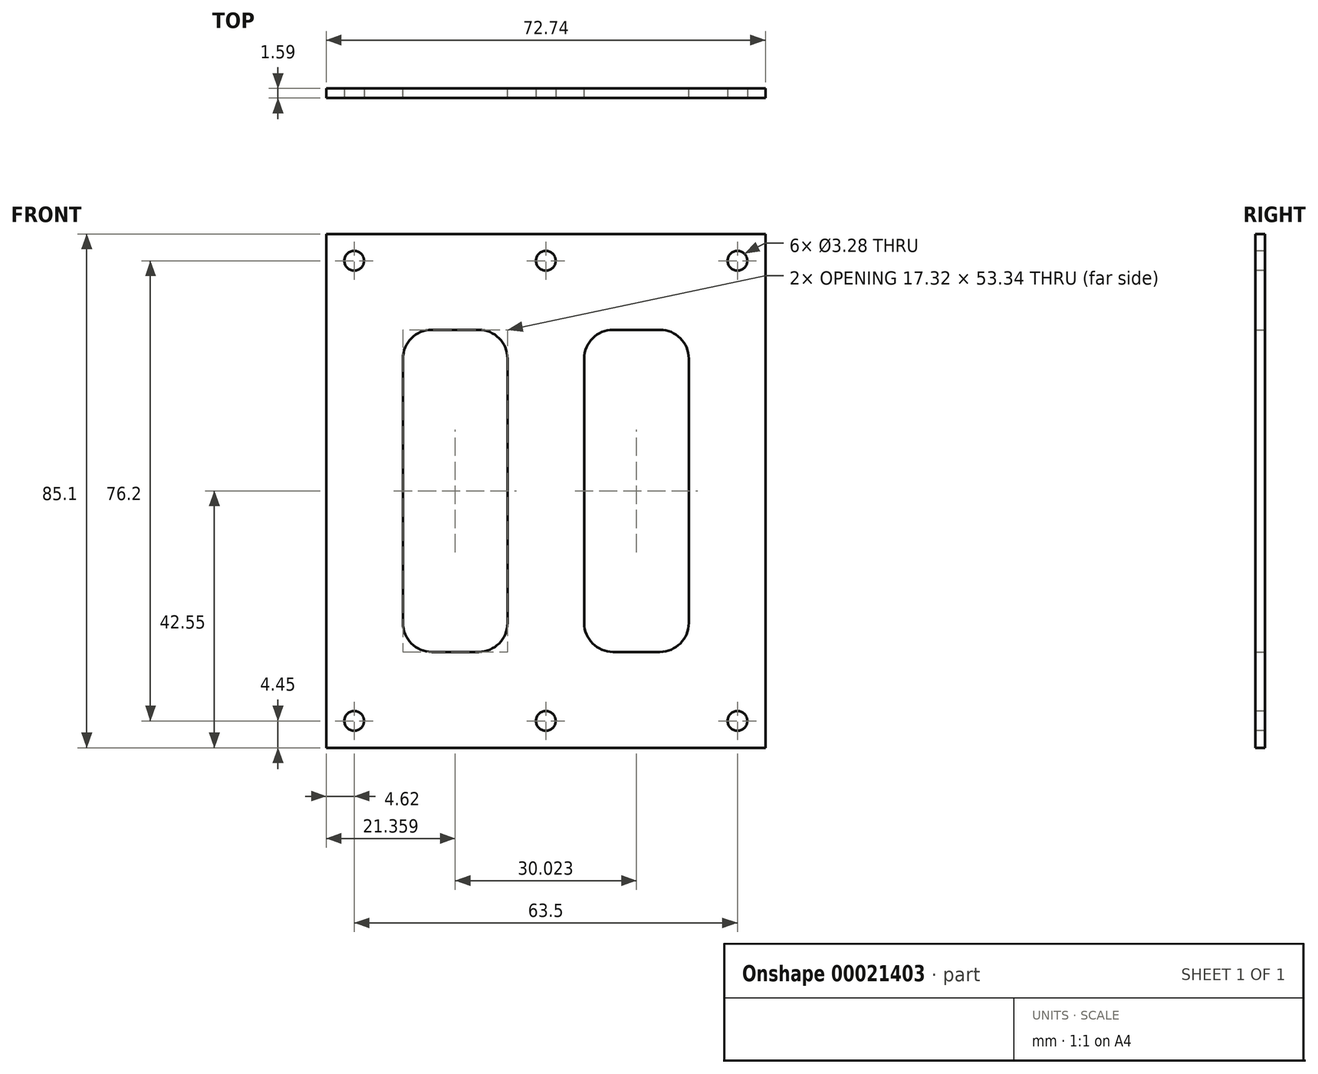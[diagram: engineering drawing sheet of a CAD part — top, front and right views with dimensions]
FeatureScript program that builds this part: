
annotation { "Feature Type Name" : "Feature", "Feature Type Description" : "" }
export const myFeature = defineFeature(function(context is Context, id is Id, definition is map)
    precondition{}
    {
        {
            var Q0;
            Q0=qCreatedBy(makeId("Front.planeOp"),FACE);
            var sketch = newSketch(context, id + "F0", { "sketchPlane" : qUnion([Q0])});
            skLineSegment(sketch, "E0.rect.bottom", {"start": v(-36.37, 42.55) * mm, "end": v(36.37, 42.55) * mm});
            skLineSegment(sketch, "E0.rect.top", {"start": v(-36.37, -42.55) * mm, "end": v(36.37, -42.55) * mm});
            skLineSegment(sketch, "E0.rect.left", {"start": v(-36.37, 42.55) * mm, "end": v(-36.37, -42.55) * mm});
            skLineSegment(sketch, "E0.rect.right", {"start": v(36.37, 42.55) * mm, "end": v(36.37, -42.55) * mm});
            skPoint(sketch, "E0.rect.middle", {"position": v(0, 0) * mm});
            skLineSegment(sketch, "E1.bottom", {"start": v(-23.67, 26.67) * mm, "end": v(-6.35, 26.67) * mm});
            skLineSegment(sketch, "E1.top", {"start": v(-23.67, -26.67) * mm, "end": v(-6.35, -26.67) * mm});
            skLineSegment(sketch, "E1.left", {"start": v(-23.67, 26.67) * mm, "end": v(-23.67, -26.67) * mm});
            skLineSegment(sketch, "E1.right", {"start": v(-6.35, 26.67) * mm, "end": v(-6.35, -26.67) * mm});
            skLineSegment(sketch, "E2.bottom", {"start": v(6.35, 26.67) * mm, "end": v(23.67, 26.67) * mm});
            skLineSegment(sketch, "E2.top", {"start": v(6.35, -26.67) * mm, "end": v(23.67, -26.67) * mm});
            skLineSegment(sketch, "E2.left", {"start": v(6.35, 26.67) * mm, "end": v(6.35, -26.67) * mm});
            skLineSegment(sketch, "E2.right", {"start": v(23.67, 26.67) * mm, "end": v(23.67, -26.67) * mm});
            skLineSegment(sketch, "E3", {"start": v(0, 0) * mm, "end": v(0, 48.33) * mm});
            skLineSegment(sketch, "E4", {"start": v(0, 0) * mm, "end": v(44.84, 0) * mm});
            skSolve(sketch);
        }
        {
            var Q0;
            {var subQ12=sQuery(id+"F0.wireOp",EDGE,"E0.rect.top");Q0=makeQuery(id+"F0.imprint","IMPRINT",FACE,{"disambiguationData":[TD([[makeQuery(id+"F0.imprint","IMPRINT",EDGE,{"derivedFrom":subQ12}),1.0]])]});}
            var Q1;
            {var subQ7=sQuery(id+"F0.wireOp",EDGE,"E2.bottom");Q1=makeQuery(id+"F0.imprint","IMPRINT",FACE,{"disambiguationData":[TD([[makeQuery(id+"F0.imprint","IMPRINT",EDGE,{"derivedFrom":subQ7}),1.0]])]});}
            extrude(context, id + "F1", {"entities" : qUnion([Q0, Q1]), "depth" : 1.59 * mm});
        }
        {
            var Q0;
            Q0=makeQuery(id+"F1.opExtrude","SWEPT_EDGE",EDGE,{"disambiguationData":[OSD([sQuery(id+"F0.wireOp",EDGE,"E2.bottom"),sQuery(id+"F0.wireOp",EDGE,"E2.right")])]});
            var Q1;
            Q1=makeQuery(id+"F1.opExtrude","SWEPT_EDGE",EDGE,{"disambiguationData":[OSD([sQuery(id+"F0.wireOp",EDGE,"E1.bottom"),sQuery(id+"F0.wireOp",EDGE,"E1.right")])]});
            var Q2;
            Q2=makeQuery(id+"F1.opExtrude","SWEPT_EDGE",EDGE,{"disambiguationData":[OSD([sQuery(id+"F0.wireOp",EDGE,"E2.bottom"),sQuery(id+"F0.wireOp",EDGE,"E2.left")])]});
            var Q3;
            Q3=makeQuery(id+"F1.opExtrude","SWEPT_EDGE",EDGE,{"disambiguationData":[OSD([sQuery(id+"F0.wireOp",EDGE,"E1.bottom"),sQuery(id+"F0.wireOp",EDGE,"E1.left")])]});
            var Q4;
            Q4=makeQuery(id+"F1.opExtrude","SWEPT_EDGE",EDGE,{"disambiguationData":[OSD([sQuery(id+"F0.wireOp",EDGE,"E2.top"),sQuery(id+"F0.wireOp",EDGE,"E2.right")])]});
            var Q5;
            Q5=makeQuery(id+"F1.opExtrude","SWEPT_EDGE",EDGE,{"disambiguationData":[OSD([sQuery(id+"F0.wireOp",EDGE,"E1.top"),sQuery(id+"F0.wireOp",EDGE,"E1.left")])]});
            var Q6;
            Q6=makeQuery(id+"F1.opExtrude","SWEPT_EDGE",EDGE,{"disambiguationData":[OSD([sQuery(id+"F0.wireOp",EDGE,"E2.top"),sQuery(id+"F0.wireOp",EDGE,"E2.left")])]});
            var Q7;
            Q7=makeQuery(id+"F1.opExtrude","SWEPT_EDGE",EDGE,{"disambiguationData":[OSD([sQuery(id+"F0.wireOp",EDGE,"E1.top"),sQuery(id+"F0.wireOp",EDGE,"E1.right")])]});
            fillet(context, id + "F2", {"entities" : qUnion([Q0, Q1, Q2, Q3, Q4, Q5, Q6, Q7]), "radius" : 4.78 * mm, "tangentPropagation" : true, "allowEdgeOverflow" : false});
        }
        {
            var Q0;
            Q0=makeQuery(id+"F1.opExtrude","CAP_FACE",FACE,{"disambiguationData":[OSD([sQuery(id+"F0.wireOp",EDGE,"E0.rect.bottom"),sQuery(id+"F0.wireOp",EDGE,"E0.rect.top"),sQuery(id+"F0.wireOp",EDGE,"E0.rect.left"),sQuery(id+"F0.wireOp",EDGE,"E0.rect.right"),sQuery(id+"F0.wireOp",EDGE,"E1.bottom"),sQuery(id+"F0.wireOp",EDGE,"E1.top"),sQuery(id+"F0.wireOp",EDGE,"E1.left"),sQuery(id+"F0.wireOp",EDGE,"E1.right"),sQuery(id+"F0.wireOp",EDGE,"E2.bottom"),sQuery(id+"F0.wireOp",EDGE,"E2.top"),sQuery(id+"F0.wireOp",EDGE,"E2.left"),sQuery(id+"F0.wireOp",EDGE,"E2.right")])],"isStart":false});
            var sketch = newSketch(context, id + "F3", { "sketchPlane" : qUnion([Q0])});
            skLineSegment(sketch, "E5.rect.bottom", {"start": v(-31.75, 38.1) * mm, "end": v(31.75, 38.1) * mm});
            skLineSegment(sketch, "E5.rect.top", {"start": v(-31.75, -38.1) * mm, "end": v(31.75, -38.1) * mm});
            skLineSegment(sketch, "E5.rect.left", {"start": v(-31.75, 38.1) * mm, "end": v(-31.75, -38.1) * mm});
            skLineSegment(sketch, "E5.rect.right", {"start": v(31.75, 38.1) * mm, "end": v(31.75, -38.1) * mm});
            skPoint(sketch, "E5.rect.middle", {"position": v(0, 0) * mm});
            skLineSegment(sketch, "E6", {"start": v(0, 38.1) * mm, "end": v(0, -38.1) * mm});
            skSolve(sketch);
        }
        {
            var Q0;
            Q0=sQuery(id+"F3.wireOp",VERTEX,"E5.rect.bottom.start");
            var Q1;
            Q1=sQuery(id+"F3.wireOp",VERTEX,"E5.rect.right.start");
            var Q2;
            Q2=sQuery(id+"F3.wireOp",VERTEX,"E5.rect.right.end");
            var Q3;
            Q3=sQuery(id+"F3.wireOp",VERTEX,"E5.rect.left.end");
            var Q4;
            Q4=sQuery(id+"F3.wireOp",VERTEX,"E6.end");
            var Q5;
            Q5=sQuery(id+"F3.wireOp",VERTEX,"E6.start");
            var Q6;
            Q6=makeQuery(id+"F1.opExtrude","SWEPT_BODY",BODY,{"disambiguationData":[OSD([sQuery(id+"F0.wireOp",EDGE,"E0.rect.bottom"),sQuery(id+"F0.wireOp",EDGE,"E0.rect.top"),sQuery(id+"F0.wireOp",EDGE,"E0.rect.left"),sQuery(id+"F0.wireOp",EDGE,"E0.rect.right"),sQuery(id+"F0.wireOp",EDGE,"E1.bottom"),sQuery(id+"F0.wireOp",EDGE,"E1.top"),sQuery(id+"F0.wireOp",EDGE,"E1.left"),sQuery(id+"F0.wireOp",EDGE,"E1.right"),sQuery(id+"F0.wireOp",EDGE,"E2.bottom"),sQuery(id+"F0.wireOp",EDGE,"E2.top"),sQuery(id+"F0.wireOp",EDGE,"E2.left"),sQuery(id+"F0.wireOp",EDGE,"E2.right")])]});
            hole(context, id + "F4", {"style" : HoleStyle.SIMPLE, "holeDiameter" : 3.28 * mm, "endStyle" : HoleEndStyle.THROUGH, "locations" : qUnion([Q0, Q1, Q2, Q3, Q4, Q5]), "scope" : qUnion([Q6])});
        }
    });
